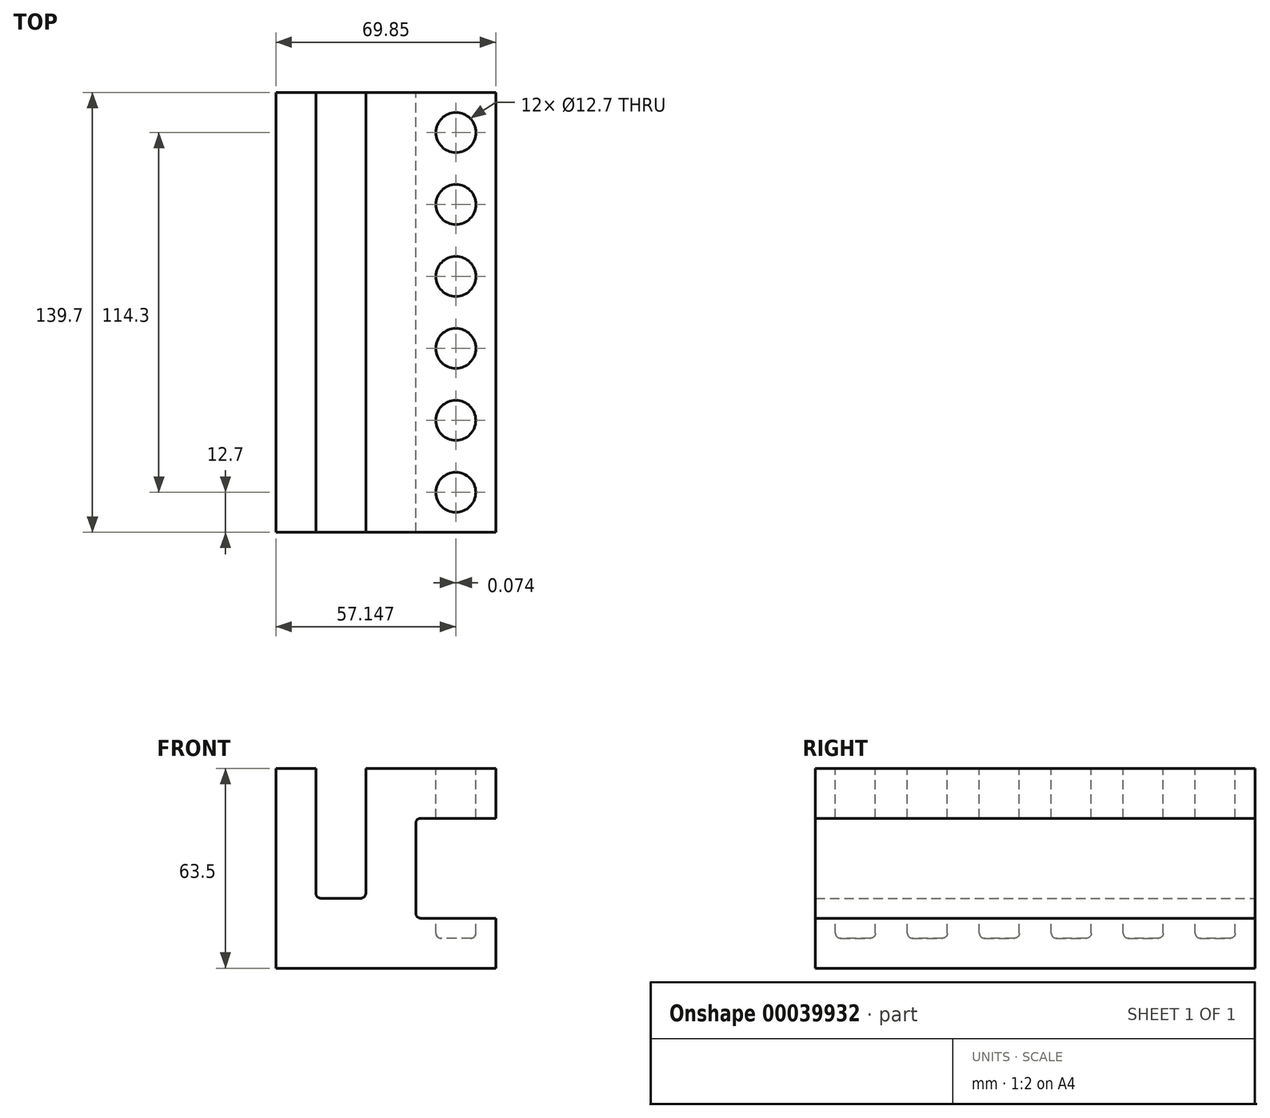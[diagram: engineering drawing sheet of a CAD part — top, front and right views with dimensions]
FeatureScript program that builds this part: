
annotation { "Feature Type Name" : "Feature", "Feature Type Description" : "" }
export const myFeature = defineFeature(function(context is Context, id is Id, definition is map)
    precondition{}
    {
        {
            var Q0;
            Q0=qCreatedBy(makeId("Front.planeOp"),FACE);
            var sketch = newSketch(context, id + "F0", { "sketchPlane" : qUnion([Q0])});
            skLineSegment(sketch, "E0", {"start": v(-36.51, 31.75) * mm, "end": v(-36.51, -31.75) * mm});
            skLineSegment(sketch, "E1", {"start": v(-36.51, -31.75) * mm, "end": v(33.34, -31.75) * mm});
            skLineSegment(sketch, "E2", {"start": v(33.34, -31.75) * mm, "end": v(33.34, -15.87) * mm});
            skLineSegment(sketch, "E3", {"start": v(33.34, -15.87) * mm, "end": v(7.94, -15.87) * mm});
            skLineSegment(sketch, "E4", {"start": v(7.94, -15.87) * mm, "end": v(7.94, 15.87) * mm});
            skLineSegment(sketch, "E5", {"start": v(7.94, 15.87) * mm, "end": v(33.34, 15.87) * mm});
            skLineSegment(sketch, "E6", {"start": v(33.34, 15.87) * mm, "end": v(33.34, 31.75) * mm});
            skLineSegment(sketch, "E7", {"start": v(33.34, 31.75) * mm, "end": v(-7.94, 31.75) * mm});
            skLineSegment(sketch, "E8", {"start": v(-7.94, 31.75) * mm, "end": v(-7.94, -9.52) * mm});
            skLineSegment(sketch, "E9", {"start": v(-7.94, -9.52) * mm, "end": v(-23.81, -9.53) * mm});
            skLineSegment(sketch, "E10", {"start": v(-23.81, -9.53) * mm, "end": v(-23.81, 31.75) * mm});
            skLineSegment(sketch, "E11", {"start": v(-23.81, 31.75) * mm, "end": v(-36.51, 31.75) * mm});
            skLineSegment(sketch, "E12", {"start": v(-7.94, 0) * mm, "end": v(7.94, 0) * mm, "construction": true});
            skSolve(sketch);
        }
        {
            var Q0;
            Q0 = qSketchRegion(id + "F0", true);
            extrude(context, id + "F1", {"entities" : qUnion([Q0]), "endBound" : BoundingType.SYMMETRIC, "depth" : 139.7 * mm});
        }
        {
            var Q0;
            Q0=makeQuery(id+"F1.opExtrude","SWEPT_FACE",FACE,{"disambiguationData":[OSD([sQuery(id+"F0.wireOp",EDGE,"E7")])]});
            var sketch = newSketch(context, id + "F2", { "sketchPlane" : qUnion([Q0])});
            skCircle(sketch, "E13", {"center": v(20.64, -57.15) * mm, "radius": 6.35 * mm});
            skCircle(sketch, "E14.1.0.0", {"center": v(20.65, -34.3) * mm, "radius": 6.35 * mm});
            skCircle(sketch, "E14.2.0.0", {"center": v(20.67, -11.43) * mm, "radius": 6.35 * mm});
            skCircle(sketch, "E14.3.0.0", {"center": v(20.68, 11.43) * mm, "radius": 6.35 * mm});
            skCircle(sketch, "E14.4.0.0", {"center": v(20.7, 34.29) * mm, "radius": 6.35 * mm});
            skCircle(sketch, "E14.5.0.0", {"center": v(20.71, 57.15) * mm, "radius": 6.35 * mm});
            skLineSegment(sketch, "E14.direction1", {"start": v(20.64, -57.15) * mm, "end": v(20.65, -34.3) * mm, "construction": true});
            skSolve(sketch);
        }
        {
            var Q0;
            Q0=makeQuery(id+"F2.imprint","IMPRINT",FACE,{"disambiguationData":[TD([[makeQuery(id+"F2.imprint","IMPRINT",EDGE,{"derivedFrom":sQuery(id+"F2.wireOp",EDGE,"E13")}),1.0]])]});
            var Q1;
            Q1=makeQuery(id+"F2.imprint","IMPRINT",FACE,{"disambiguationData":[TD([[makeQuery(id+"F2.imprint","IMPRINT",EDGE,{"derivedFrom":sQuery(id+"F2.wireOp",EDGE,"E14.1.0.0")}),1.0]])]});
            var Q2;
            Q2=makeQuery(id+"F2.imprint","IMPRINT",FACE,{"disambiguationData":[TD([[makeQuery(id+"F2.imprint","IMPRINT",EDGE,{"derivedFrom":sQuery(id+"F2.wireOp",EDGE,"E14.2.0.0")}),1.0]])]});
            var Q3;
            Q3=makeQuery(id+"F2.imprint","IMPRINT",FACE,{"disambiguationData":[TD([[makeQuery(id+"F2.imprint","IMPRINT",EDGE,{"derivedFrom":sQuery(id+"F2.wireOp",EDGE,"E14.3.0.0")}),1.0]])]});
            var Q4;
            Q4=makeQuery(id+"F2.imprint","IMPRINT",FACE,{"disambiguationData":[TD([[makeQuery(id+"F2.imprint","IMPRINT",EDGE,{"derivedFrom":sQuery(id+"F2.wireOp",EDGE,"E14.4.0.0")}),1.0]])]});
            var Q5;
            Q5=makeQuery(id+"F2.imprint","IMPRINT",FACE,{"disambiguationData":[TD([[makeQuery(id+"F2.imprint","IMPRINT",EDGE,{"derivedFrom":sQuery(id+"F2.wireOp",EDGE,"E14.5.0.0")}),1.0]])]});
            extrude(context, id + "F3", {"entities" : qUnion([Q0, Q1, Q2, Q3, Q4, Q5]), "operationType" : NewBodyOperationType.REMOVE, "oppositeDirection" : true, "depth" : 53.97 * mm});
        }
        {
            var Q0;
            Q0=makeQuery(id+"F1.opExtrude","SWEPT_EDGE",EDGE,{"disambiguationData":[OSD([sQuery(id+"F0.wireOp",EDGE,"E3"),sQuery(id+"F0.wireOp",EDGE,"E4")])]});
            var Q1;
            Q1=makeQuery(id+"F1.opExtrude","SWEPT_EDGE",EDGE,{"disambiguationData":[OSD([sQuery(id+"F0.wireOp",EDGE,"E4"),sQuery(id+"F0.wireOp",EDGE,"E5")])]});
            var Q2;
            Q2=makeQuery(id+"F1.opExtrude","SWEPT_EDGE",EDGE,{"disambiguationData":[OSD([sQuery(id+"F0.wireOp",EDGE,"E9"),sQuery(id+"F0.wireOp",EDGE,"E10")])]});
            var Q3;
            Q3=makeQuery(id+"F1.opExtrude","SWEPT_EDGE",EDGE,{"disambiguationData":[OSD([sQuery(id+"F0.wireOp",EDGE,"E8"),sQuery(id+"F0.wireOp",EDGE,"E9")])]});
            fillet(context, id + "F4", {"entities" : qUnion([Q0, Q1, Q2, Q3]), "radius" : 1.59 * mm, "tangentPropagation" : true, "allowEdgeOverflow" : false});
        }
        {
            var Q0;
            Q0=makeQuery(id+"F3.boolean.opBoolean","COPY",EDGE,{"derivedFrom":makeQuery(id+"F3.opExtrude","CAP_EDGE",EDGE,{"disambiguationData":[OSD([sQuery(id+"F2.wireOp",EDGE,"E14.5.0.0")])],"isStart":false})});
            var Q1;
            Q1=makeQuery(id+"F3.boolean.opBoolean","COPY",EDGE,{"derivedFrom":makeQuery(id+"F3.opExtrude","CAP_EDGE",EDGE,{"disambiguationData":[OSD([sQuery(id+"F2.wireOp",EDGE,"E14.4.0.0")])],"isStart":false})});
            var Q2;
            Q2=makeQuery(id+"F3.boolean.opBoolean","COPY",EDGE,{"derivedFrom":makeQuery(id+"F3.opExtrude","CAP_EDGE",EDGE,{"disambiguationData":[OSD([sQuery(id+"F2.wireOp",EDGE,"E14.3.0.0")])],"isStart":false})});
            var Q3;
            Q3=makeQuery(id+"F3.boolean.opBoolean","COPY",EDGE,{"derivedFrom":makeQuery(id+"F3.opExtrude","CAP_EDGE",EDGE,{"disambiguationData":[OSD([sQuery(id+"F2.wireOp",EDGE,"E14.2.0.0")])],"isStart":false})});
            var Q4;
            Q4=makeQuery(id+"F3.boolean.opBoolean","COPY",EDGE,{"derivedFrom":makeQuery(id+"F3.opExtrude","CAP_EDGE",EDGE,{"disambiguationData":[OSD([sQuery(id+"F2.wireOp",EDGE,"E14.1.0.0")])],"isStart":false})});
            var Q5;
            Q5=makeQuery(id+"F3.boolean.opBoolean","COPY",EDGE,{"derivedFrom":makeQuery(id+"F3.opExtrude","CAP_EDGE",EDGE,{"disambiguationData":[OSD([sQuery(id+"F2.wireOp",EDGE,"E13")])],"isStart":false})});
            fillet(context, id + "F5", {"entities" : qUnion([Q0, Q1, Q2, Q3, Q4, Q5]), "radius" : 1.59 * mm, "tangentPropagation" : true, "allowEdgeOverflow" : false});
        }
    });
